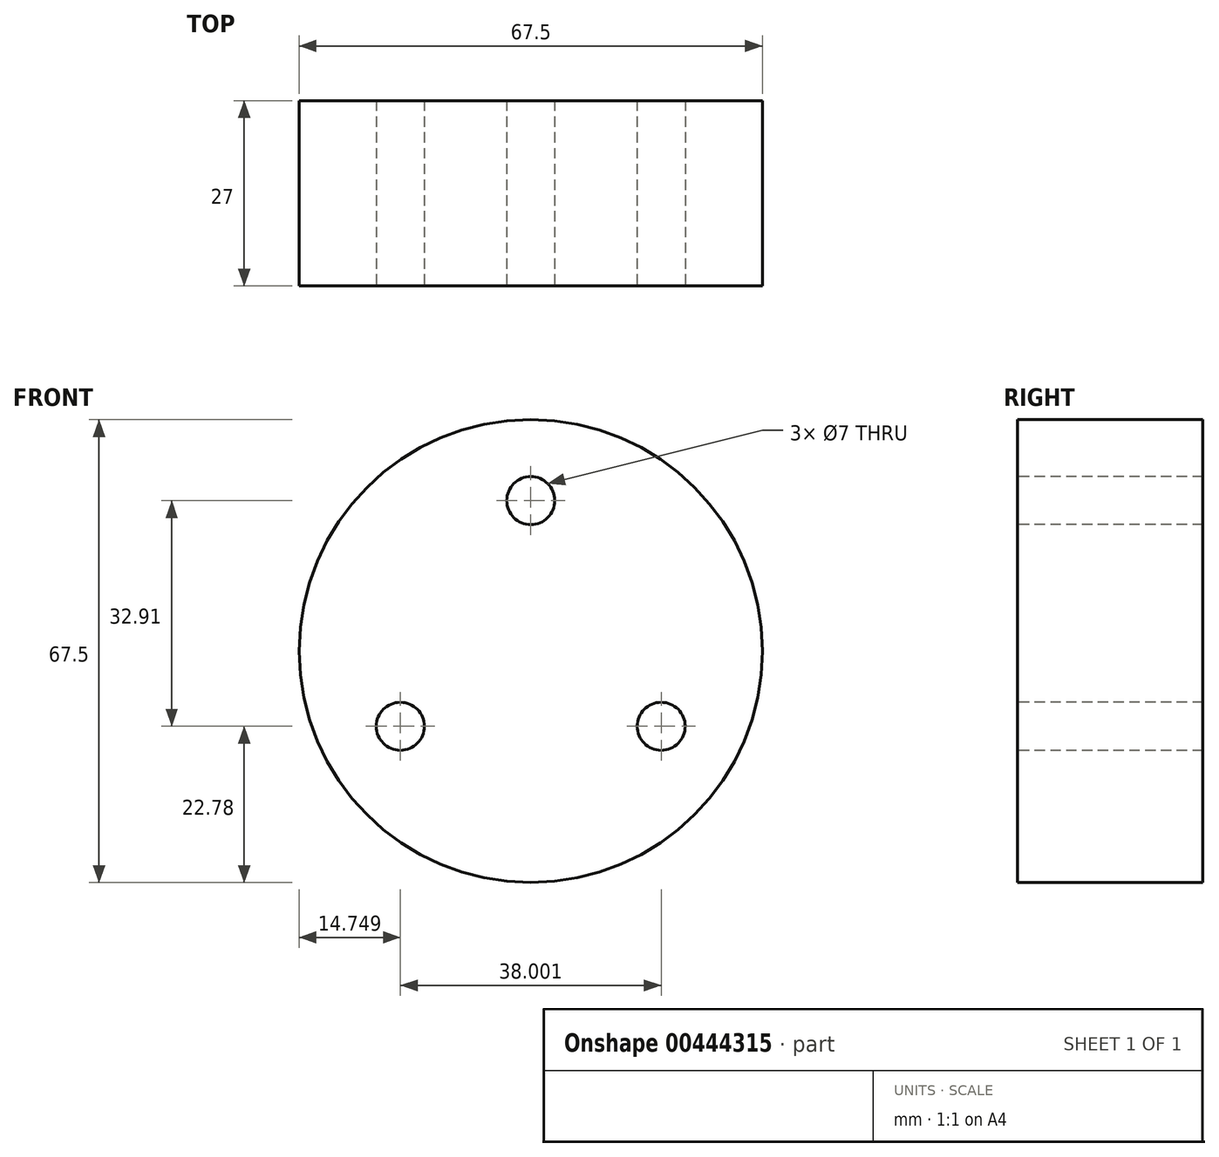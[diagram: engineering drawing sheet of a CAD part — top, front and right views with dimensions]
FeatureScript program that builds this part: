
annotation { "Feature Type Name" : "Feature", "Feature Type Description" : "" }
export const myFeature = defineFeature(function(context is Context, id is Id, definition is map)
    precondition{}
    {
        {
            var Q0;
            Q0=qCreatedBy(makeId("Front.planeOp"),FACE);
            var sketch = newSketch(context, id + "F0", { "sketchPlane" : qUnion([Q0])});
            skCircle(sketch, "E0", {"center": v(0, 0) * mm, "radius": 33.75 * mm});
            skSolve(sketch);
        }
        {
            var Q0;
            Q0=makeQuery(id+"F0.imprint","IMPRINT",FACE,{"disambiguationData":[TD([[makeQuery(id+"F0.imprint","IMPRINT",EDGE,{"derivedFrom":sQuery(id+"F0.wireOp",EDGE,"E0")}),1.0]])]});
            extrude(context, id + "F1", {"entities" : qUnion([Q0]), "oppositeDirection" : true, "depth" : 27 * mm});
        }
        {
            var Q0;
            Q0=makeQuery(id+"F1.opExtrude","CAP_FACE",FACE,{"disambiguationData":[OSD([sQuery(id+"F0.wireOp",EDGE,"E0")])],"isStart":true});
            var sketch = newSketch(context, id + "F2", { "sketchPlane" : qUnion([Q0])});
            skCircle(sketch, "E1", {"center": v(0, 21.94) * mm, "radius": 3.5 * mm});
            skCircle(sketch, "E2.1.0", {"center": v(-19, -10.97) * mm, "radius": 3.5 * mm});
            skCircle(sketch, "E2.2.0", {"center": v(19, -10.97) * mm, "radius": 3.5 * mm});
            skPoint(sketch, "E2.center", {"position": v(0, 0) * mm});
            skSolve(sketch);
        }
        {
            var Q0;
            Q0 = qSketchRegion(id + "F2", true);
            extrude(context, id + "F3", {"entities" : qUnion([Q0]), "operationType" : NewBodyOperationType.REMOVE, "oppositeDirection" : true, "depth" : 27 * mm});
        }
    });
